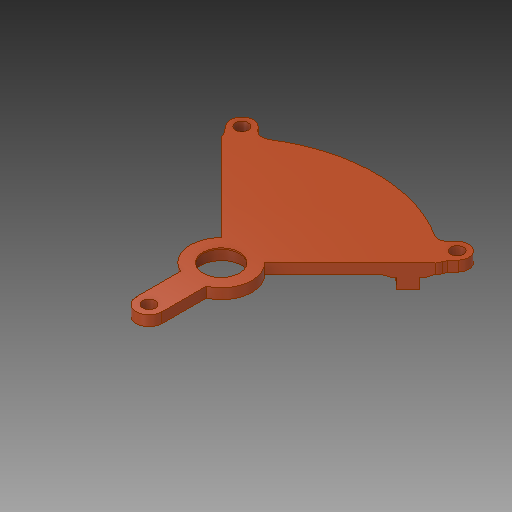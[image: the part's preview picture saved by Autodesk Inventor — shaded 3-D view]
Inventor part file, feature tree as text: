
AUTODESK INVENTOR PART (.ipt)
format: ipt  version: 2018.2 (Build 222227000, 227)  size: 272,896 bytes
history: native  units: mm
features: sketch x9, extrude x4, sweep x3, mirror x2, fillet x2, projected_geometry x1
ambient origin geometry x8: Origin, YZ Plane, XZ Plane, XY Plane, X Axis, Y Axis, Z Axis, Center Point
bodies: Solid1 (feature_tree)
feature tree (21):
  extrude  "Extrusion1"  Depth=0.15mm
  sketch  "Sketch2"  dims[d2=5.0mm d5=28.0mm]
  sweep  "Sweep1"
  sweep  "Sweep2"
  extrude  "Extrusion2"  Depth=60.0mm
  mirror  "Mirror1"
  sweep  "Sweep3"
  mirror  "Mirror2"
  fillet  "Fillet1"  Radius=5.0mm
  extrude  "Extrusion3"  TaperAngle=15.0deg  [1 undecoded]
  extrude  "Extrusion4"  Depth=3.5mm
  fillet  "Fillet2"  [1 undecoded]
  sketch  "Sketch1"  dims[d0=15.875mm d1=0.15mm]
  sketch  "3D Sketch1"
  sketch  "3D Sketch2"
  sketch  "Sketch3"  dims[d8=4.0mm d9=4.0mm d10=0.0mm]
  projected_geometry  "Projected Loop1"
  sketch  "Sketch4"  dims[d11=90.0deg d12=60.0mm]
  sketch  "Sketch5"  dims[d13=10.0mm d14=1.0mm d15=5.0mm]
  sketch  "Sketch6"  dims[d16=1.5mm d17=15.0deg]
  sketch  "Sketch7"  dims[d18=2.0mm d19=3.5mm d20=0.0mm d21=0.0mm d22=0.0mm d23=0.0mm d24=5.0mm d25=2.0mm d27=4.0mm d28=0.0mm d29=4.0mm d30=5.0mm d31=0.0mm d32=0.0mm d33=6.981317mm d34=65.0mm d35=4.0mm d37=0.5mm d38=0.0mm d39=2.0mm d40=1.0mm d41=0.0mm d42=4.0mm d43=1.0mm]
note: 2 required parameter values undecoded (feature->parameter linkage not recoverable at this tier; creation-order binding heuristic only, values carry confidence <= 0.55)
